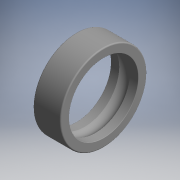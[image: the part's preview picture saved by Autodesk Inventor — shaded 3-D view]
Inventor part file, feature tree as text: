
AUTODESK INVENTOR PART (.ipt)
format: ipt  version: 2017.3 (Build 213256000, 256)  size: 140,800 bytes
history: native  units: mm (DEFAULTED — no unit token found)
features: revolve x1, sketch x1
ambient origin geometry x8: Origin, YZ Plane, XZ Plane, XY Plane, X Axis, Y Axis, Z Axis, Center Point
bodies: Solid1 (feature_tree)
feature tree (2):
  revolve  "Revolution1"  [1 undecoded]
  sketch  "Sketch_1"  dims[d0=360.0deg]
note: 1 required parameter value undecoded (feature->parameter linkage not recoverable at this tier; creation-order binding heuristic only, values carry confidence <= 0.55)
